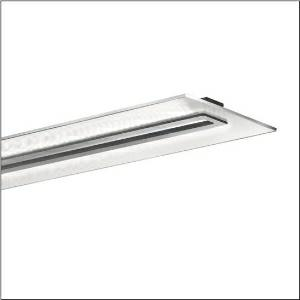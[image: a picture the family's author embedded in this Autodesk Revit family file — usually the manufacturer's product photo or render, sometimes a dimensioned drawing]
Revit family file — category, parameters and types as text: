
# Revit family: vega_11_5mn238dle003
name_source: partatom
category: Lighting Fixtures
units: mm (PartAtom-declared; Revit-internal decimal feet)

## family parameters
Cut with Voids When Loaded = No
Host = Face
Light Source = No
Part Type = Normal
Room Calculation Point = No
Round Connector Dimension = Use Diameter
Shared = No

## types (1)
- --- (1 x LED 3000K / CRI = 80 (unbekannt), 7300 lm, 3000K)
    Apparent Load = 62 VA
    CIE Flux Codes = 61 86 97 62 100
    Color Rendering = 80
    Color Temperature = 3000K
    Default Elevation = 1800 mm
    Description = Vega 11, office luminaire, primary light control with prismatic reflector, of PMMA, transparent prismatic structure, CAT 2 (L<= 1500cd/m²), light emission: direct/indirect distribution, primary light characteristic: symmetric, installation type: suspended mounting, surface-mounted, LED, rated luminous flux: 7.300lm, luminous efficacy: 118lm/W, light colour: 830, colour temperature: 3000K, control gear: DALI, with terminal, 3+2-pole, max. 2.5mm², mains connection: 230V, AC, 50Hz, connection cable inclusive, cable length: 1,5m, rated input power: 62W, luminaire housing, rectangular, rounded, of aluminium section, anodised, metallic grey (RAL 9006), length: 1.250mm, width: 350mm, height: 43mm, luminaire housing, lower part, of aluminium section, anodised, metallic grey (RAL 9006), of PC, grey, protection rating (complete): IP20, insulation class (complete): insulation class I (protective earthing), certification: CE, standard: EN 50419, packaging unit: 1 piece
    Height = 40 mm  [stored 0.131234 ft]
    Lamp = 1 x LED 3000K / CRI >= 80 (unbekannt)
    Lamp Light Flux = 7300 lm
    Lamp count = 1
    Length = 1250 mm
    Luminous efficacy = 118 lm/W
    Manufacturer = Siteco
    ModVariant = No
    Model = 5MN238DLE003
    Mounting Place = Ceiling
    Mounting Type = Pendant
    Number of Poles = 1
    OnlyDefault = Yes
    Power Factor = 1
    Product Name = Vega 11
    Product group = office luminaire | ceiling pendant
    ProductGroupID = 903
    Protection Class = Protection class I
    Protection Degree = IP 20
    RLX_Detail_Level = 1
    RLX_Emergency_Light_Flux = 0 lm
    RLX_Emergency_Type = 0
    RLX_Emergency_Type_DB = No
    RlxData = <blob elided: 62681 chars, md5=88d58b0e>
    Socket = socket
    Standby Power = 0 W
    System Light Flux = 7300 lm
    System Power = 62 W
    Type Comments = factory setting: luminous flux: 100 % | dim-lin: 254 | 460 mA
    Type Image = l_1004807.jpg
    URL = http://relux.com
    VarID = @adj_197023
    Voltage = 0 V
    Weight = 0.00 kg
    Width = 350 mm

note: [stored X ft] marks values corroborated as IEEE doubles in the binary element streams (Revit-internal decimal feet)

## geometry (parser evidence)
native form markers: Blend x4, Sweep x12
no freeform markers — native parametric forms only
